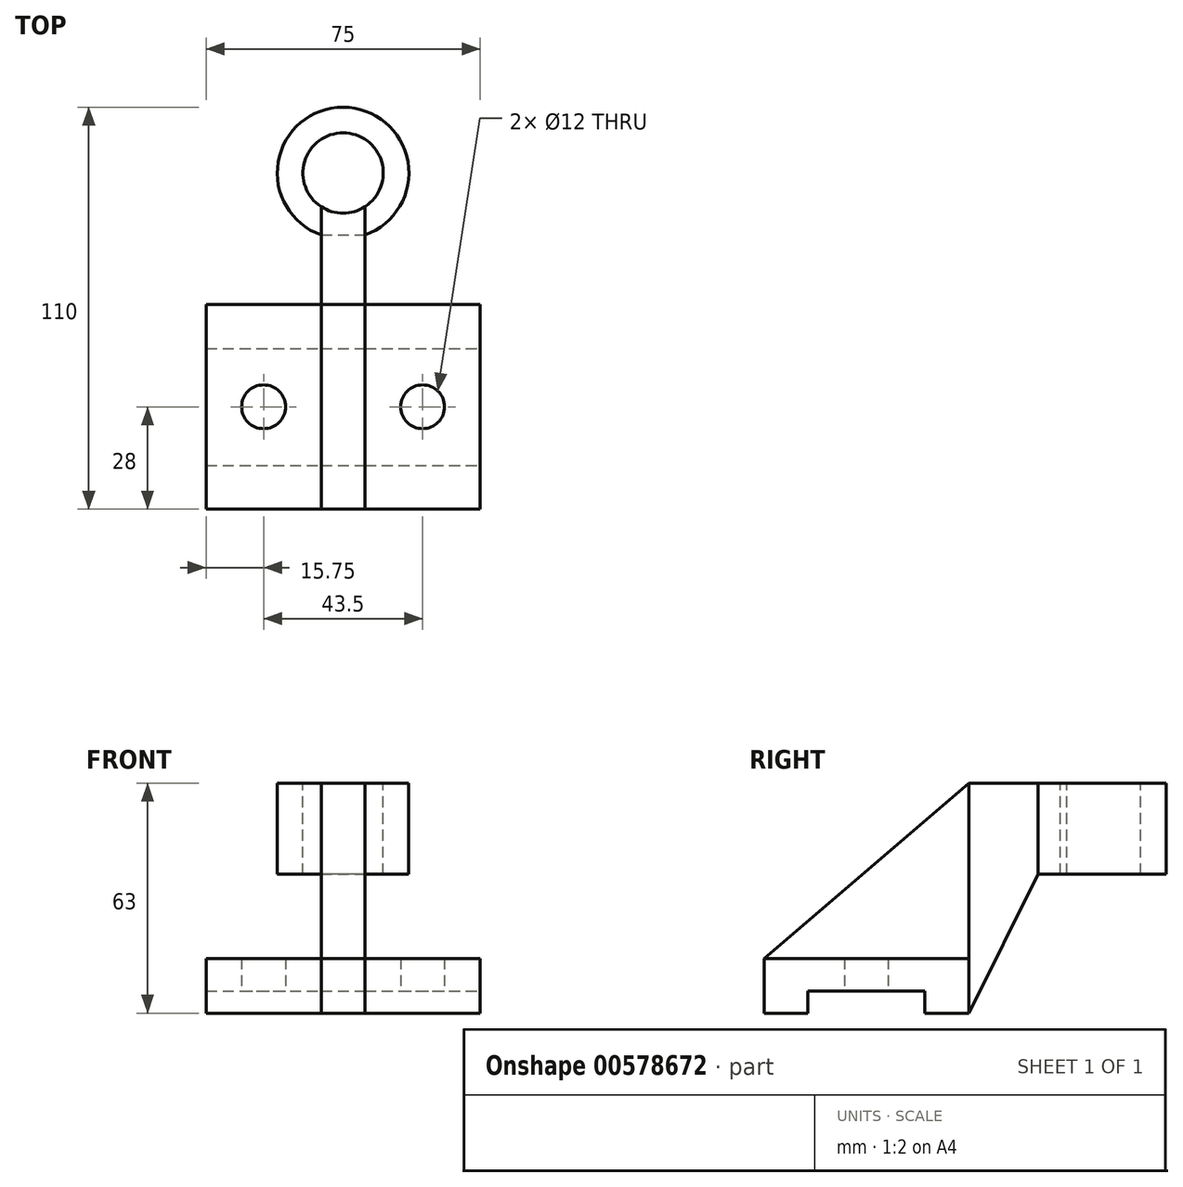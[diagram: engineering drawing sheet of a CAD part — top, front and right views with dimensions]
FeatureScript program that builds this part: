
annotation { "Feature Type Name" : "Feature", "Feature Type Description" : "" }
export const myFeature = defineFeature(function(context is Context, id is Id, definition is map)
    precondition{}
    {
        {
            var Q0;
            Q0=qCreatedBy(makeId("Top.planeOp"),FACE);
            var sketch = newSketch(context, id + "F0", { "sketchPlane" : qUnion([Q0])});
            skLineSegment(sketch, "E0.bottom", {"start": v(37.5, 28) * mm, "end": v(-37.5, 28) * mm});
            skLineSegment(sketch, "E0.top", {"start": v(37.5, -28) * mm, "end": v(-37.5, -28) * mm});
            skLineSegment(sketch, "E0.left", {"start": v(37.5, 28) * mm, "end": v(37.5, -28) * mm});
            skLineSegment(sketch, "E0.right", {"start": v(-37.5, 28) * mm, "end": v(-37.5, -28) * mm});
            skPoint(sketch, "E0.middle", {"position": v(0, 0) * mm});
            skLineSegment(sketch, "E1", {"start": v(0, 28) * mm, "end": v(0, -28) * mm});
            skLineSegment(sketch, "E2", {"start": v(6, 28) * mm, "end": v(6, -28) * mm});
            skLineSegment(sketch, "E3", {"start": v(-6, 28) * mm, "end": v(-6, -28) * mm});
            skLineSegment(sketch, "E4", {"start": v(-6, 28) * mm, "end": v(-37.5, 28) * mm});
            skLineSegment(sketch, "E5", {"start": v(6, 28) * mm, "end": v(37.5, 28) * mm});
            skCircle(sketch, "E6", {"center": v(-21.75, 0) * mm, "radius": 6 * mm});
            skPoint(sketch, "E6.centerSnap0", {"position": v(-21.75, 28) * mm});
            skCircle(sketch, "E7", {"center": v(21.75, 0) * mm, "radius": 6 * mm});
            skPoint(sketch, "E7.centerSnap0", {"position": v(21.75, 28) * mm});
            skSolve(sketch);
        }
        {
            var Q0;
            {var subQ0=sQuery(id+"F0.wireOp",EDGE,"E0.right");Q0=makeQuery(id+"F0.imprint","IMPRINT",FACE,{"disambiguationData":[TD([[makeQuery(id+"F0.imprint","IMPRINT",EDGE,{"derivedFrom":subQ0}),1.0]])]});}
            var Q1;
            {var subQ1=sQuery(id+"F0.wireOp",EDGE,"E0.left");Q1=makeQuery(id+"F0.imprint","IMPRINT",FACE,{"disambiguationData":[TD([[makeQuery(id+"F0.imprint","IMPRINT",EDGE,{"derivedFrom":subQ1}),-1.0]])]});}
            extrude(context, id + "F1", {"entities" : qUnion([Q0, Q1]), "depth" : 15 * mm, "offsetDistance" : 25 * mm});
        }
        {
            var Q0;
            {var subQ2=sQuery(id+"F0.wireOp",EDGE,"E1");Q0=makeQuery(id+"F0.imprint","IMPRINT",FACE,{"disambiguationData":[TD([[makeQuery(id+"F0.imprint","IMPRINT",EDGE,{"derivedFrom":subQ2}),1.0]])]});}
            var Q1;
            {var subQ2=sQuery(id+"F0.wireOp",EDGE,"E1");Q1=makeQuery(id+"F0.imprint","IMPRINT",FACE,{"disambiguationData":[TD([[makeQuery(id+"F0.imprint","IMPRINT",EDGE,{"derivedFrom":subQ2}),-1.0]])]});}
            extrude(context, id + "F2", {"entities" : qUnion([Q0, Q1]), "depth" : 63 * mm, "offsetDistance" : 25 * mm});
        }
        {
            var Q0;
            Q0=makeQuery(id+"F2.opExtrude","SWEPT_FACE",FACE,{"disambiguationData":[OSD([sQuery(id+"F0.wireOp",EDGE,"E2")])]});
            var sketch = newSketch(context, id + "F3", { "sketchPlane" : qUnion([Q0])});
            skLineSegment(sketch, "E8.0.0", {"start": v(-28, 0) * mm, "end": v(28, 0) * mm});
            skLineSegment(sketch, "E8.0.1", {"start": v(28, 0) * mm, "end": v(28, 63) * mm});
            skLineSegment(sketch, "E8.0.2", {"start": v(28, 63) * mm, "end": v(-28, 63) * mm});
            skLineSegment(sketch, "E8.0.3", {"start": v(-28, 63) * mm, "end": v(-28, 0) * mm});
            skLineSegment(sketch, "E9.0", {"start": v(28, 15) * mm, "end": v(-28, 15) * mm});
            skLineSegment(sketch, "E10", {"start": v(28, 63) * mm, "end": v(-28, 15) * mm});
            skSolve(sketch);
        }
        {
            var Q0;
            {var subQ0=sQuery(id+"F3.wireOp",EDGE,"E8.0.2");Q0=makeQuery(id+"F3.imprint","IMPRINT",FACE,{"disambiguationData":[TD([[makeQuery(id+"F3.imprint","IMPRINT",EDGE,{"derivedFrom":subQ0}),1.0]])]});}
            extrude(context, id + "F4", {"entities" : qUnion([Q0]), "operationType" : NewBodyOperationType.REMOVE, "oppositeDirection" : true, "depth" : 25 * mm, "offsetDistance" : 25 * mm});
        }
        {
            var Q0;
            Q0=makeQuery(id+"F2.opExtrude","SWEPT_FACE",FACE,{"disambiguationData":[OSD([sQuery(id+"F0.wireOp",EDGE,"E0.bottom")])]});
            extrude(context, id + "F5", {"entities" : qUnion([Q0]), "depth" : 36 * mm, "offsetDistance" : 25 * mm});
        }
        {
            var Q0;
            Q0=makeQuery(id+"F5.opExtrude","SWEPT_FACE",FACE,{"disambiguationData":[OSD([sQuery(id+"F0.wireOp",EDGE,"E0.bottom"),sQuery(id+"F3.wireOp",EDGE,"E8.0.1"),sQuery(id+"F3.wireOp",EDGE,"E8.0.2"),sQuery(id+"F3.wireOp",EDGE,"E10")])]});
            var sketch = newSketch(context, id + "F6", { "sketchPlane" : qUnion([Q0])});
            skCircle(sketch, "E11", {"center": v(0, 64) * mm, "radius": 11 * mm});
            skCircle(sketch, "E12", {"center": v(0, 64) * mm, "radius": 18 * mm});
            skSolve(sketch);
        }
        {
            var Q0;
            {var subQ1=sQuery(id+"F3.wireOp",EDGE,"E10");var subQ2=sQuery(id+"F3.wireOp",EDGE,"E8.0.2");var subQ3=sQuery(id+"F3.wireOp",EDGE,"E8.0.1");var subQ4=sQuery(id+"F0.wireOp",EDGE,"E0.bottom");var subQ11=makeQuery(id+"F5.opExtrude","CAP_EDGE",EDGE,{"disambiguationData":[OSD([subQ4,subQ3,subQ2,subQ1])],"isStart":false});Q0=makeQuery(id+"F6.imprint","IMPRINT",FACE,{"disambiguationData":[TD([[makeQuery(id+"F6.imprint","IMPRINT",EDGE,{"derivedFrom":subQ11}),1.0]])]});}
            extrude(context, id + "F7", {"entities" : qUnion([Q0]), "operationType" : NewBodyOperationType.REMOVE, "oppositeDirection" : true, "depth" : 91.3 * mm, "offsetDistance" : 25 * mm});
        }
        {
            var Q0;
            {var subQ0=sQuery(id+"F6.wireOp",EDGE,"E11");var subQ1=sQuery(id+"F0.wireOp",EDGE,"E0.bottom");var subQ4=sQuery(id+"F0.wireOp",EDGE,"E4");var subQ5=sQuery(id+"F0.wireOp",EDGE,"E3");var subQ6=makeQuery(id+"F5.opExtrude","SWEPT_EDGE",EDGE,{"disambiguationData":[OSD([subQ1,subQ5,subQ4]),TDD([makeQuery(id+"F2.opExtrude","CAP_VERTEX",VERTEX,{"disambiguationData":[OSD([subQ1,subQ5,subQ4])],"isStart":false})])]});var subQ7=makeQuery(id+"F6.imprint","INTERSECT",VERTEX,{"derivedFrom":[subQ6,subQ0]});Q0=makeQuery(id+"F6.imprint","IMPRINT",FACE,{"disambiguationData":[TD([[makeQuery(id+"F6.imprint","IMPRINT",EDGE,{"disambiguationData":[TD([[subQ7,1.0]])],"derivedFrom":subQ0}),-1.0]])]});}
            extrude(context, id + "F8", {"entities" : qUnion([Q0]), "oppositeDirection" : true, "depth" : 25 * mm, "offsetDistance" : 25 * mm});
        }
        {
            var Q0;
            Q0=makeQuery(id+"F5.opExtrude","SWEPT_FACE",FACE,{"disambiguationData":[OSD([sQuery(id+"F0.wireOp",EDGE,"E0.bottom"),sQuery(id+"F0.wireOp",EDGE,"E2"),sQuery(id+"F0.wireOp",EDGE,"E5")])]});
            var sketch = newSketch(context, id + "F9", { "sketchPlane" : qUnion([Q0])});
            skLineSegment(sketch, "E13", {"start": v(82, 63) * mm, "end": v(82, 38) * mm});
            skPoint(sketch, "E14.0", {"position": v(47.03, 38) * mm});
            skLineSegment(sketch, "E15.0.0", {"start": v(28, 0) * mm, "end": v(54.78, 0) * mm});
            skLineSegment(sketch, "E15.0.1", {"start": v(54.78, 0) * mm, "end": v(54.78, 63) * mm});
            skLineSegment(sketch, "E15.0.2", {"start": v(54.78, 63) * mm, "end": v(28, 63) * mm});
            skLineSegment(sketch, "E15.0.3", {"start": v(28, 63) * mm, "end": v(28, 0) * mm});
            skLineSegment(sketch, "E16.0.0", {"start": v(-28, 0) * mm, "end": v(28, 0) * mm});
            skLineSegment(sketch, "E16.0.1", {"start": v(28, 0) * mm, "end": v(28, 15) * mm});
            skLineSegment(sketch, "E16.0.2", {"start": v(28, 15) * mm, "end": v(-28, 15) * mm});
            skLineSegment(sketch, "E16.0.3", {"start": v(-28, 15) * mm, "end": v(-28, 0) * mm});
            skLineSegment(sketch, "E17", {"start": v(47.03, 38) * mm, "end": v(28, 0) * mm});
            skLineSegment(sketch, "E18", {"start": v(47.03, 38) * mm, "end": v(54.78, 38) * mm});
            skLineSegment(sketch, "E19", {"start": v(54.78, 38) * mm, "end": v(54.78, 0) * mm});
            skSolve(sketch);
        }
        {
            var Q0;
            Q0=makeQuery(id+"F9.imprint","IMPRINT",FACE,{"disambiguationData":[TD([[makeQuery(id+"F9.imprint","IMPRINT",EDGE,{"derivedFrom":sQuery(id+"F9.wireOp",EDGE,"E15.0.0")}),-1.0]])]});
            extrude(context, id + "F10", {"entities" : qUnion([Q0]), "operationType" : NewBodyOperationType.REMOVE, "oppositeDirection" : true, "depth" : 25 * mm, "offsetDistance" : 25 * mm});
        }
        {
            var Q0;
            Q0=makeQuery(id+"F1.opExtrude","SWEPT_FACE",FACE,{"disambiguationData":[OSD([sQuery(id+"F0.wireOp",EDGE,"E0.left")])]});
            var sketch = newSketch(context, id + "F11", { "sketchPlane" : qUnion([Q0])});
            skLineSegment(sketch, "E20.bottom", {"start": v(-16, 0) * mm, "end": v(16, 0) * mm});
            skLineSegment(sketch, "E20.top", {"start": v(-16, 6) * mm, "end": v(16, 6) * mm});
            skLineSegment(sketch, "E20.left", {"start": v(-16, 0) * mm, "end": v(-16, 6) * mm});
            skLineSegment(sketch, "E20.right", {"start": v(16, 0) * mm, "end": v(16, 6) * mm});
            skSolve(sketch);
        }
        {
            var Q0;
            Q0 = qSketchRegion(id + "F11", true);
            extrude(context, id + "F12", {"entities" : qUnion([Q0]), "operationType" : NewBodyOperationType.REMOVE, "oppositeDirection" : true, "depth" : 107.5 * mm, "offsetDistance" : 25 * mm});
        }
    });
